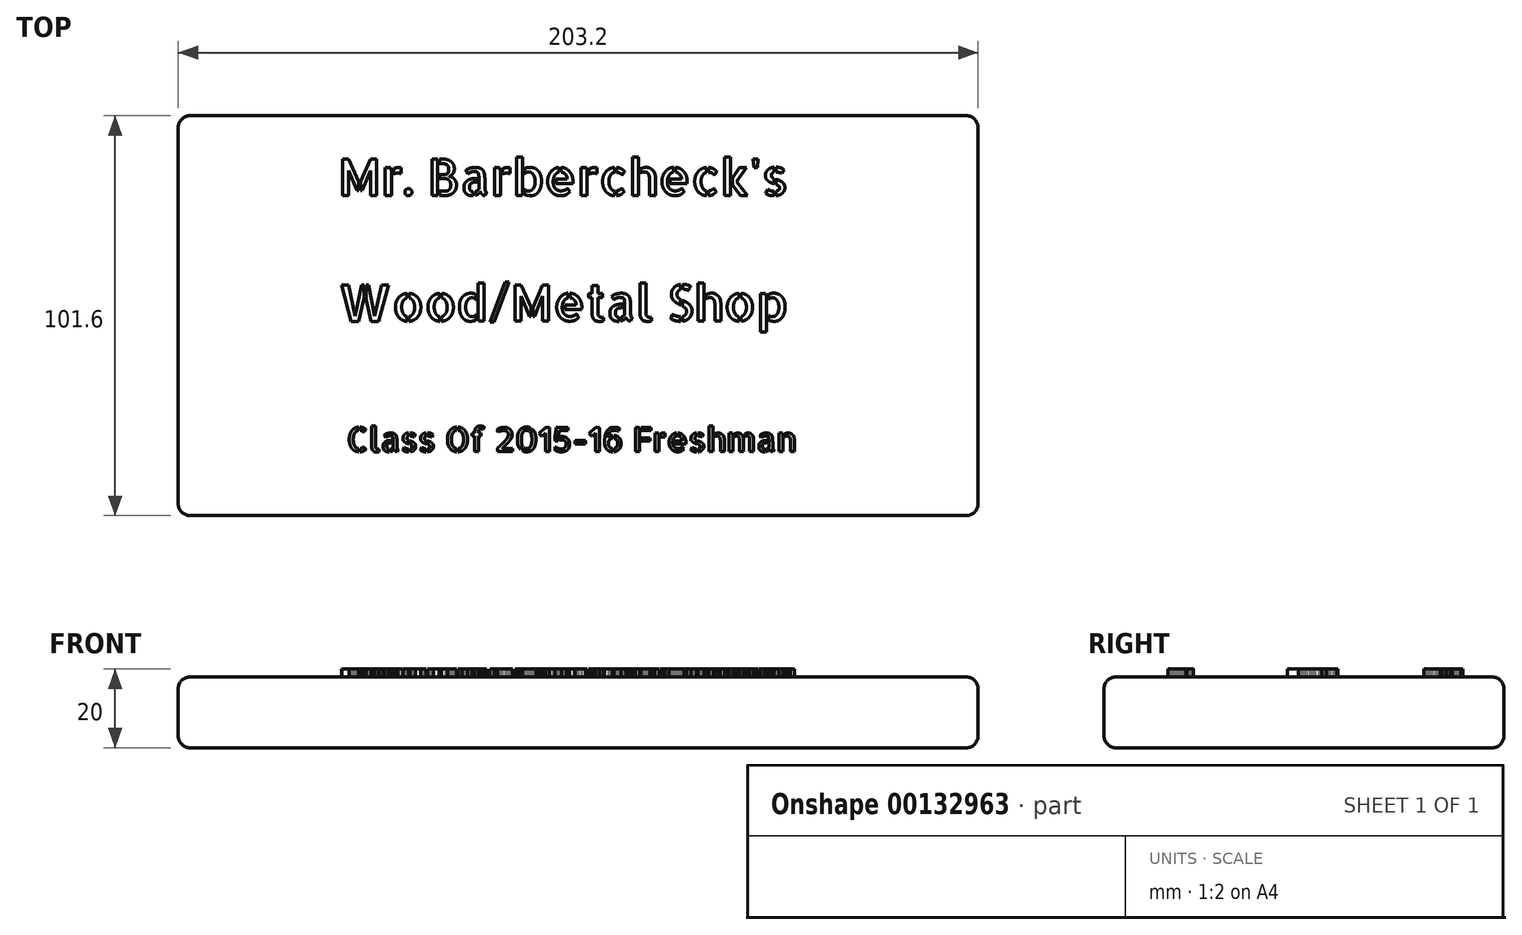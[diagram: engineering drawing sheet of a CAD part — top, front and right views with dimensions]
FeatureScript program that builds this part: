
annotation { "Feature Type Name" : "Feature", "Feature Type Description" : "" }
export const myFeature = defineFeature(function(context is Context, id is Id, definition is map)
    precondition{}
    {
        {
            var Q0;
            Q0=qCreatedBy(makeId("Top.planeOp"),FACE);
            var sketch = newSketch(context, id + "F0", { "sketchPlane" : qUnion([Q0])});
            skLineSegment(sketch, "E0.bottom", {"start": v(-97.78, 57.49) * mm, "end": v(105.42, 57.49) * mm});
            skLineSegment(sketch, "E0.top", {"start": v(-97.78, -44.11) * mm, "end": v(105.42, -44.11) * mm});
            skLineSegment(sketch, "E0.left", {"start": v(-97.78, 57.49) * mm, "end": v(-97.78, -44.11) * mm});
            skLineSegment(sketch, "E0.right", {"start": v(105.42, 57.49) * mm, "end": v(105.42, -44.11) * mm});
            skSolve(sketch);
        }
        {
            var Q0;
            Q0=makeQuery(id+"F0.imprint","IMPRINT",FACE,{"disambiguationData":[TD([[makeQuery(id+"F0.imprint","IMPRINT",EDGE,{"derivedFrom":sQuery(id+"F0.wireOp",EDGE,"E0.bottom")}),-1.0]])]});
            extrude(context, id + "F1", {"entities" : qUnion([Q0]), "depth" : 18 * mm});
        }
        {
            var Q0;
            Q0=makeQuery(id+"F1.opExtrude","CAP_FACE",FACE,{"disambiguationData":[OSD([sQuery(id+"F0.wireOp",EDGE,"E0.bottom"),sQuery(id+"F0.wireOp",EDGE,"E0.top"),sQuery(id+"F0.wireOp",EDGE,"E0.left"),sQuery(id+"F0.wireOp",EDGE,"E0.right")])],"isStart":false});
            fillet(context, id + "F2", {"entities" : qUnion([Q0]), "radius" : 3 * mm, "tangentPropagation" : true, "allowEdgeOverflow" : false});
        }
        {
            var Q0;
            Q0=makeQuery(id+"F1.opExtrude","SWEPT_FACE",FACE,{"disambiguationData":[OSD([sQuery(id+"F0.wireOp",EDGE,"E0.top")])]});
            fillet(context, id + "F3", {"entities" : qUnion([Q0]), "radius" : 3 * mm, "tangentPropagation" : true, "allowEdgeOverflow" : false});
        }
        {
            var Q0;
            Q0=makeQuery(id+"F1.opExtrude","SWEPT_FACE",FACE,{"disambiguationData":[OSD([sQuery(id+"F0.wireOp",EDGE,"E0.left")])]});
            var Q1;
            Q1=makeQuery(id+"F1.opExtrude","SWEPT_FACE",FACE,{"disambiguationData":[OSD([sQuery(id+"F0.wireOp",EDGE,"E0.bottom")])]});
            fillet(context, id + "F4", {"entities" : qUnion([Q0, Q1]), "radius" : 3 * mm, "tangentPropagation" : true, "allowEdgeOverflow" : false});
        }
        {
            var Q0;
            Q0=makeQuery(id+"F1.opExtrude","CAP_EDGE",EDGE,{"disambiguationData":[OSD([sQuery(id+"F0.wireOp",EDGE,"E0.right")])],"isStart":true});
            fillet(context, id + "F5", {"entities" : qUnion([Q0]), "radius" : 3 * mm, "tangentPropagation" : true, "allowEdgeOverflow" : false});
        }
        {
            var Q0;
            Q0=makeQuery(id+"F1.opExtrude","CAP_FACE",FACE,{"disambiguationData":[OSD([sQuery(id+"F0.wireOp",EDGE,"E0.bottom"),sQuery(id+"F0.wireOp",EDGE,"E0.top"),sQuery(id+"F0.wireOp",EDGE,"E0.left"),sQuery(id+"F0.wireOp",EDGE,"E0.right")])],"isStart":false});
            var sketch = newSketch(context, id + "F6", { "sketchPlane" : qUnion([Q0])});
            skCircle(sketch, "E1", {"center": v(-82.08, 41.79) * mm, "radius": 3.18 * mm});
            skCircle(sketch, "E2", {"center": v(89.72, 41.79) * mm, "radius": 3.18 * mm});
            skSolve(sketch);
        }
        {
            var Q0;
            Q0=makeQuery(id+"F6.imprint","IMPRINT",FACE,{"disambiguationData":[TD([[makeQuery(id+"F6.imprint","IMPRINT",EDGE,{"derivedFrom":sQuery(id+"F6.wireOp",EDGE,"E1")}),-1.0]])]});
            var sketch = newSketch(context, id + "F7", { "sketchPlane" : qUnion([Q0])});
            skText(sketch, "E3", { "text": "Mr. Barbercheck\'s", "fontName": "AllertaStencil-Regular.ttf"});
            skText(sketch, "E4", { "text": "Wood/Metal Shop", "fontName": "AllertaStencil-Regular.ttf"});
            skText(sketch, "E5", { "text": "Class Of 2015-16 Freshman", "fontName": "AllertaStencil-Regular.ttf"});
            const initialGuessF7  = {"E3": [-0.05715, 0.0372, 1, 0, 0.00929], "E4": [-0.05715, 0.0053, 1, 0, 0.0092], "E5": [-0.055, -0.02788, 1, 0, 0.00617]};
            skSetInitialGuess(sketch, initialGuessF7);
            skSolve(sketch);
        }
        {
            var Q0;
            Q0 = qSketchRegion(id + "F7", true);
            extrude(context, id + "F8", {"entities" : qUnion([Q0]), "operationType" : NewBodyOperationType.ADD, "depth" : 2 * mm});
        }
    });
